# Revit family: Urinal_Touchless_AC-Wall_Mount-KOHLER-BARDON-K-4915T
name_source: partatom
category: Plumbing Fixtures
revit_build: Autodesk Revit 2017 (Build: 20160225_1515(x64)
units: mm (PartAtom-declared; Revit-internal decimal feet)

## family parameters
Cut with Voids When Loaded = No
Host = Face
OmniClass Number = 23.31.21.00
OmniClass Title = Urinals
Part Type = Normal
Room Calculation Point = No
Round Connector Dimension = Use Diameter
Shared = No

## types (3) — shared parameters
ADA Compliant = No
Apparent Load = 0 VA
Assembly Code = D2010200
CW Connection = Yes
Cold Water Inlet = Cold Water Inlet
Date Modified = 09/02/2021
Default Elevation = 0"
Electrical Note = One Dedicated Circuit Required
Eletrical Connector = Yes
Finish = Kohler-Vitreous_China-0-White
Flow Rate = 0 GPM
HW Connection = No
Height = 30 3/4"
Hot Water Inlet = Hot Water Inlet
Length = 14 1/4"
Manufacturer = KOHLER Co.
Master Format 2014 = 22 41 13.16
Master Format 2014 Name = Residential Urinals
Material = Vitreous China
Pressure = 0.00 psi
Product Documentation Link = https://files.kohler.com.cn
Product Name = BARDON
Product Page URL = https://www.kohler.com.cn
URL = http://www.kohler.com.cn
Vent Connection = No
Voltage = 220 V
Waste Connection = Yes
Waste Water Outlet = Waste Water Outlet
WaterSense Certified = No
Width = 18 1/4"

## per-type parameters (varying)
| type | Automatic Sensor Urinal | Connector Distance | Description | Flush Rate- GPF | Flush Rate- LPF | Model | Type | Water Saving Automatic Sensor Urinal |
| 2.5 LPF, 0-White | Yes | 4 15/16" | automatic sensor urinal | 0.66 GPF | 2.5 LPF | K-4915T-C05-0 | 1 | No |
| 1.0 LPF, 0-White | No | 5 3/4" | Barton water-saving automatic sensor urinal | 0.26 GPF | 1.0 LPF | K-4915T-WC05-0 | 2 | Yes |
| 0.5 LPF, 0-White | No | 5 3/4" | Barton super water-saving automatic sensor urinal | 0.13 GPF | 0.5 LPF | K-4915T-YC05-0 | 3 | Yes |

## geometry (parser evidence)
native form markers: Sweep x5
no freeform markers — native parametric forms only
